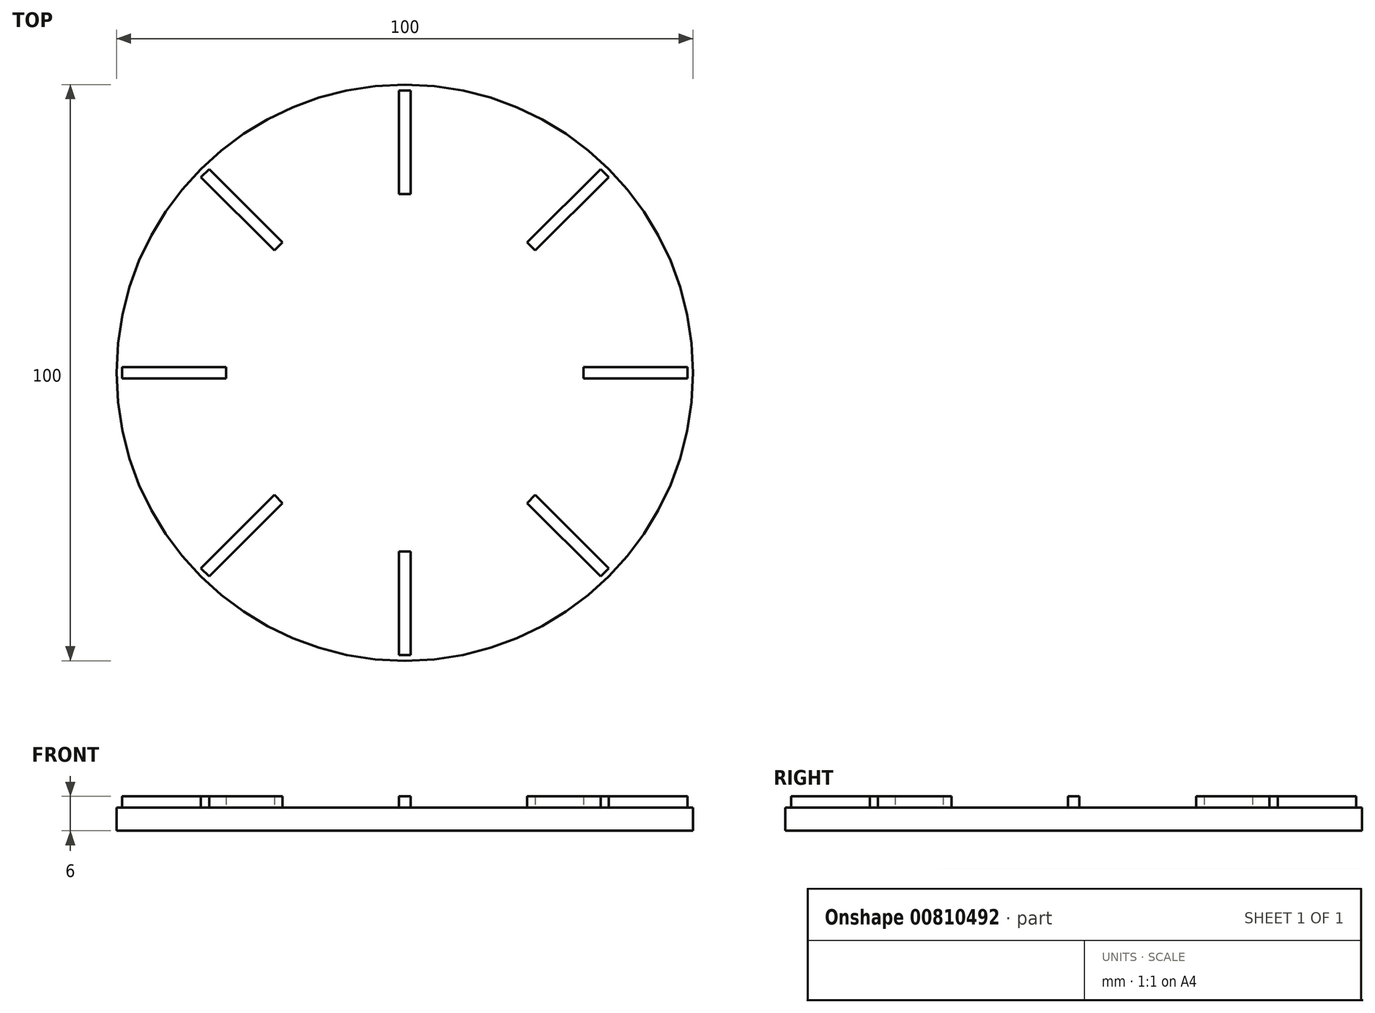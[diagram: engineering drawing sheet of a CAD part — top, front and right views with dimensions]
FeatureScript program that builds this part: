
annotation { "Feature Type Name" : "Feature", "Feature Type Description" : "" }
export const myFeature = defineFeature(function(context is Context, id is Id, definition is map)
    precondition{}
    {
        {
            var Q0;
            Q0=qCreatedBy(makeId("Top.planeOp"),FACE);
            var sketch = newSketch(context, id + "F0", { "sketchPlane" : qUnion([Q0])});
            skCircle(sketch, "E0", {"center": v(0, 0) * mm, "radius": 50 * mm});
            skSolve(sketch);
        }
        {
            var Q0;
            Q0 = qSketchRegion(id + "F0", true);
            extrude(context, id + "F1", {"entities" : qUnion([Q0]), "depth" : 4 * mm, "offsetDistance" : 25 * mm});
        }
        {
            var Q0;
            Q0=makeQuery(id+"F1.opExtrude","CAP_FACE",FACE,{"disambiguationData":[OSD([sQuery(id+"F0.wireOp",EDGE,"E0")])],"isStart":false});
            var sketch = newSketch(context, id + "F2", { "sketchPlane" : qUnion([Q0])});
            skLineSegment(sketch, "E1.bottom", {"start": v(1, 31) * mm, "end": v(-1, 31) * mm});
            skLineSegment(sketch, "E1.top", {"start": v(1, 49) * mm, "end": v(-1, 49) * mm});
            skLineSegment(sketch, "E1.left", {"start": v(1, 31) * mm, "end": v(1, 49) * mm});
            skLineSegment(sketch, "E1.right", {"start": v(-1, 31) * mm, "end": v(-1, 49) * mm});
            skPoint(sketch, "E1.middle", {"position": v(0, 40) * mm});
            skLineSegment(sketch, "E2.1.0", {"start": v(-21.21, 22.63) * mm, "end": v(-33.94, 35.36) * mm});
            skLineSegment(sketch, "E2.1.1", {"start": v(-22.63, 21.21) * mm, "end": v(-35.36, 33.94) * mm});
            skLineSegment(sketch, "E2.1.2", {"start": v(-21.21, 22.63) * mm, "end": v(-22.63, 21.21) * mm});
            skLineSegment(sketch, "E2.1.3", {"start": v(-33.94, 35.36) * mm, "end": v(-35.36, 33.94) * mm});
            skLineSegment(sketch, "E2.2.0", {"start": v(-31, 1) * mm, "end": v(-49, 1) * mm});
            skLineSegment(sketch, "E2.2.1", {"start": v(-31, -1) * mm, "end": v(-49, -1) * mm});
            skLineSegment(sketch, "E2.2.2", {"start": v(-31, 1) * mm, "end": v(-31, -1) * mm});
            skLineSegment(sketch, "E2.2.3", {"start": v(-49, 1) * mm, "end": v(-49, -1) * mm});
            skLineSegment(sketch, "E2.3.0", {"start": v(-22.63, -21.21) * mm, "end": v(-35.36, -33.94) * mm});
            skLineSegment(sketch, "E2.3.1", {"start": v(-21.21, -22.63) * mm, "end": v(-33.94, -35.36) * mm});
            skLineSegment(sketch, "E2.3.2", {"start": v(-22.63, -21.21) * mm, "end": v(-21.21, -22.63) * mm});
            skLineSegment(sketch, "E2.3.3", {"start": v(-35.36, -33.94) * mm, "end": v(-33.94, -35.36) * mm});
            skLineSegment(sketch, "E2.4.0", {"start": v(-1, -31) * mm, "end": v(-1, -49) * mm});
            skLineSegment(sketch, "E2.4.1", {"start": v(1, -31) * mm, "end": v(1, -49) * mm});
            skLineSegment(sketch, "E2.4.2", {"start": v(-1, -31) * mm, "end": v(1, -31) * mm});
            skLineSegment(sketch, "E2.4.3", {"start": v(-1, -49) * mm, "end": v(1, -49) * mm});
            skLineSegment(sketch, "E2.5.0", {"start": v(21.21, -22.63) * mm, "end": v(33.94, -35.36) * mm});
            skLineSegment(sketch, "E2.5.1", {"start": v(22.63, -21.21) * mm, "end": v(35.36, -33.94) * mm});
            skLineSegment(sketch, "E2.5.2", {"start": v(21.21, -22.63) * mm, "end": v(22.63, -21.21) * mm});
            skLineSegment(sketch, "E2.5.3", {"start": v(33.94, -35.36) * mm, "end": v(35.36, -33.94) * mm});
            skLineSegment(sketch, "E2.6.0", {"start": v(31, -1) * mm, "end": v(49, -1) * mm});
            skLineSegment(sketch, "E2.6.1", {"start": v(31, 1) * mm, "end": v(49, 1) * mm});
            skLineSegment(sketch, "E2.6.2", {"start": v(31, -1) * mm, "end": v(31, 1) * mm});
            skLineSegment(sketch, "E2.6.3", {"start": v(49, -1) * mm, "end": v(49, 1) * mm});
            skLineSegment(sketch, "E2.7.0", {"start": v(22.63, 21.21) * mm, "end": v(35.36, 33.94) * mm});
            skLineSegment(sketch, "E2.7.1", {"start": v(21.21, 22.63) * mm, "end": v(33.94, 35.36) * mm});
            skLineSegment(sketch, "E2.7.2", {"start": v(22.63, 21.21) * mm, "end": v(21.21, 22.63) * mm});
            skLineSegment(sketch, "E2.7.3", {"start": v(35.36, 33.94) * mm, "end": v(33.94, 35.36) * mm});
            skPoint(sketch, "E2.center", {"position": v(0, 0) * mm});
            skSolve(sketch);
        }
        {
            var Q0;
            Q0=makeQuery(id+"F2.imprint","IMPRINT",FACE,{"disambiguationData":[TD([[makeQuery(id+"F2.imprint","IMPRINT",EDGE,{"derivedFrom":sQuery(id+"F2.wireOp",EDGE,"E2.1.0")}),1.0]])]});
            var Q1;
            Q1=makeQuery(id+"F2.imprint","IMPRINT",FACE,{"disambiguationData":[TD([[makeQuery(id+"F2.imprint","IMPRINT",EDGE,{"derivedFrom":sQuery(id+"F2.wireOp",EDGE,"E1.bottom")}),-1.0]])]});
            var Q2;
            Q2=makeQuery(id+"F2.imprint","IMPRINT",FACE,{"disambiguationData":[TD([[makeQuery(id+"F2.imprint","IMPRINT",EDGE,{"derivedFrom":sQuery(id+"F2.wireOp",EDGE,"E2.7.0")}),1.0]])]});
            var Q3;
            Q3=makeQuery(id+"F2.imprint","IMPRINT",FACE,{"disambiguationData":[TD([[makeQuery(id+"F2.imprint","IMPRINT",EDGE,{"derivedFrom":sQuery(id+"F2.wireOp",EDGE,"E2.6.0")}),1.0]])]});
            var Q4;
            Q4=makeQuery(id+"F2.imprint","IMPRINT",FACE,{"disambiguationData":[TD([[makeQuery(id+"F2.imprint","IMPRINT",EDGE,{"derivedFrom":sQuery(id+"F2.wireOp",EDGE,"E2.5.0")}),1.0]])]});
            var Q5;
            Q5=makeQuery(id+"F2.imprint","IMPRINT",FACE,{"disambiguationData":[TD([[makeQuery(id+"F2.imprint","IMPRINT",EDGE,{"derivedFrom":sQuery(id+"F2.wireOp",EDGE,"E2.4.0")}),1.0]])]});
            var Q6;
            Q6=makeQuery(id+"F2.imprint","IMPRINT",FACE,{"disambiguationData":[TD([[makeQuery(id+"F2.imprint","IMPRINT",EDGE,{"derivedFrom":sQuery(id+"F2.wireOp",EDGE,"E2.3.0")}),1.0]])]});
            var Q7;
            Q7=makeQuery(id+"F2.imprint","IMPRINT",FACE,{"disambiguationData":[TD([[makeQuery(id+"F2.imprint","IMPRINT",EDGE,{"derivedFrom":sQuery(id+"F2.wireOp",EDGE,"E2.2.0")}),1.0]])]});
            extrude(context, id + "F3", {"entities" : qUnion([Q0, Q1, Q2, Q3, Q4, Q5, Q6, Q7]), "operationType" : NewBodyOperationType.ADD, "depth" : 2 * mm, "offsetDistance" : 25 * mm});
        }
    });
